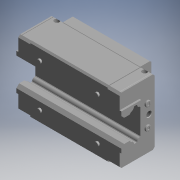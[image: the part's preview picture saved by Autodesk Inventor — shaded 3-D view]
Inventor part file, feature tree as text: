
AUTODESK INVENTOR PART (.ipt)
format: ipt  version: 2022 (Build 260153000, 153)  size: 429,568 bytes
history: native  units: mm (DEFAULTED — no unit token found)
features: sketch x39, extrude x22, other x21, revolve x10, hole x7, pattern_linear x1
ambient origin geometry x8: Origin, YZ Plane, XZ Plane, XY Plane, X Axis, Y Axis, Z Axis, Center Point
bodies: Solid1 (feature_tree)
feature tree (100):
  extrude  "Extrusion1"  Depth=2.0mm
  hole  "Hole1"  [1 undecoded]
  pattern_linear  "Rectangular Pattern1"  [2 undecoded]
  extrude  "Extrusion2"  [1 undecoded]
  extrude  "Extrusion3"  [1 undecoded]
  extrude  "Extrusion4"  [1 undecoded]
  extrude  "Extrusion5"  [1 undecoded]
  extrude  "Extrusion6"  [1 undecoded]
  extrude  "Extrusion7"  [1 undecoded]
  hole  "Hole2"  [1 undecoded]
  hole  "Hole3"  [1 undecoded]
  extrude  "Extrusion8"  [1 undecoded]
  extrude  "Extrusion9"  [1 undecoded]
  extrude  "Extrusion10"  [1 undecoded]
  extrude  "Extrusion11"  [1 undecoded]
  extrude  "Extrusion12"  [1 undecoded]
  revolve  "Revolution1"  [1 undecoded]
  revolve  "Revolution2"  [1 undecoded]
  revolve  "Revolution3"  [1 undecoded]
  revolve  "Revolution4"  [1 undecoded]
  extrude  "Extrusion13"  [1 undecoded]
  extrude  "Extrusion14"  [1 undecoded]
  extrude  "Extrusion15"  [1 undecoded]
  extrude  "Extrusion16"  [1 undecoded]
  extrude  "Extrusion17"  [1 undecoded]
  extrude  "Extrusion18"  [1 undecoded]
  extrude  "Extrusion19"  [1 undecoded]
  extrude  "Extrusion20"  [1 undecoded]
  extrude  "Extrusion21"  [1 undecoded]
  extrude  "Extrusion22"  [1 undecoded]
  hole  "Hole4"  [1 undecoded]
  hole  "Hole5"  [1 undecoded]
  revolve  "Revolution5"  [1 undecoded]
  revolve  "Revolution6"  [1 undecoded]
  revolve  "Revolution7"  [1 undecoded]
  revolve  "Revolution8"  [1 undecoded]
  revolve  "Revolution9"  [1 undecoded]
  hole  "Hole6"  [1 undecoded]
  revolve  "Revolution10"  [1 undecoded]
  hole  "Hole7"  [1 undecoded]
  other  "4TRACK_XY"
  other  "4TRACK_YZ"
  other  "4TRACK_ZX"
  other  "4TRACK_X"
  other  "4TRACK_Y"
  other  "4TRACK_Z"
  other  "4TRACK_Center"
  other  "niple_XY"
  other  "niple_YZ"
  other  "niple_ZX"
  other  "niple_X"
  other  "niple_Y"
  other  "niple_Z"
  other  "niple_Center"
  other  "niple2_XY"
  other  "niple2_YZ"
  other  "niple2_ZX"
  other  "niple2_X"
  other  "niple2_Y"
  other  "niple2_Z"
  other  "niple2_Center"
  sketch  "Sketch_22"  dims[d53=360.0deg]
  sketch  "Sketch2"  dims[d2=6.647mm d3=12.6765mm d4=8.0mm d5=2.0mm d6=90.0deg d7=14.4mm d8=120.0deg d9=20.0mm d11=50.0mm d12=20.0mm d14=50.0mm]
  sketch  "Sketch_7"  dims[d23=10.5mm d24=0.0mm]
  sketch  "Sketch_2"  dims[d15=11.0mm d16=0.0mm d17=3.5mm d18=0.0mm]
  sketch  "Sketch_8"  dims[d25=10.5mm d26=0.0mm]
  sketch  "Sketch_42"  dims[d82=4.917mm d83=5.5415mm d84=6.0mm d85=2.0mm d86=90.0deg d87=6.0mm d88=120.0deg]
  sketch  "Sketch_106"  dims[d102=5.2mm d103=6.0mm d104=4.0mm d105=2.0mm d106=90.0deg d107=5.2mm d108=0.0mm]
  sketch  "Sketch_107"  dims[d109=0.0mm d110=0.0mm]
  sketch  "Sketch9"  dims[d27=6.2mm d28=6.0mm d29=4.0mm d30=2.0mm d31=90.0deg d32=1.0mm d33=0.0mm]
  sketch  "Sketch10"  dims[d34=6.2mm d35=6.0mm d36=4.0mm d37=2.0mm d38=90.0deg d39=1.0mm d40=0.0mm]
  sketch  "Sketch_1"  dims[d0=80.4mm d1=0.0mm]
  sketch  "Sketch_6"  dims[d21=3.5mm d22=0.0mm]
  sketch  "Sketch_20"  dims[d51=360.0deg]
  sketch  "Sketch_21"  dims[d52=360.0deg]
  sketch  "Sketch_65"  dims[d93=360.0deg]
  sketch  "Sketch_4"  dims[d19=11.0mm d20=0.0mm]
  sketch  "Sketch_14"  dims[d45=2.0mm d46=0.0mm]
  sketch  "Sketch_15"  dims[d47=2.0mm d48=0.0mm]
  sketch  "Sketch_16"  dims[d49=109.4mm d50=0.0mm]
  sketch  "Sketch_24"  dims[d54=360.0deg]
  sketch  "Sketch_25"  dims[d55=0.75mm d56=0.0mm]
  sketch  "Sketch_26"  dims[d57=0.75mm d58=0.0mm]
  sketch  "Sketch_27"  dims[d59=0.75mm d60=0.0mm]
  sketch  "Sketch_12"  dims[d41=2.0mm d42=0.0mm]
  sketch  "Sketch_13"  dims[d43=2.0mm d44=0.0mm]
  sketch  "Sketch_45"  dims[d89=360.0deg]
  sketch  "Sketch_46"  dims[d90=360.0deg]
  sketch  "Sketch_47"  dims[d91=360.0deg]
  sketch  "Sketch_48"  dims[d92=360.0deg]
  sketch  "Sketch30"  dims[d61=0.75mm d62=0.0mm]
  sketch  "Sketch31"  dims[d63=68.0mm d64=0.0mm]
  sketch  "Sketch_34"  dims[d65=68.0mm d66=0.0mm]
  sketch  "Sketch_35"  dims[d67=47.5mm d68=0.0mm]
  sketch  "Sketch_37"  dims[d69=47.5mm d70=0.0mm]
  sketch  "Sketch_38"  dims[d73=47.5mm d74=0.0mm]
  sketch  "Sketch_94"  dims[d94=5.2mm d95=6.0mm d96=4.0mm d97=2.0mm d98=90.0deg d99=5.2mm d100=0.0mm]
  sketch  "Sketch37"  dims[d71=47.5mm d72=0.0mm]
  sketch  "Sketch_96"  dims[d101=360.0deg]
  sketch  "Sketch39"  dims[d75=4.917mm d76=5.5415mm d77=6.0mm d78=2.0mm d79=90.0deg d80=6.0mm d81=120.0deg]
note: 40 required parameter values undecoded (feature->parameter linkage not recoverable at this tier; creation-order binding heuristic only, values carry confidence <= 0.55)
